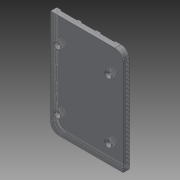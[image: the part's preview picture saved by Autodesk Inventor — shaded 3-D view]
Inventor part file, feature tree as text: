
AUTODESK INVENTOR PART (.ipt)
format: ipt  version: 2015 (Build 190159000, 159)  size: 218,624 bytes
history: native  units: mm
features: extrude x6, chamfer x5, other x4, fillet x1, shell x1, imported_body x1
ambient origin geometry x8: Origin, YZ Plane, XZ Plane, XY Plane, X Axis, Y Axis, Z Axis, Center Point
bodies: Solid1 (feature_tree)
feature tree (18):
  extrude  "baseBody"  Depth=70.0mm
  fillet  "filletBaseBody"  Radius=100.0mm
  shell  "shellBaseBody"  Thickness=50.0mm
  extrude  "borderCase"  Depth=35.0mm
  extrude  "frontHoles"  TaperAngle=0.0deg  [1 undecoded]
  extrude  "lateralHoles"  TaperAngle=0.0deg  [1 undecoded]
  other  "baseScrewHolders"
  extrude  "screwHolders"  Depth=5.0mm TaperAngle=0.0deg
  extrude  "screwHoles"  Depth=8.0mm
  chamfer  "screwHolderChamfler1"  Distance=2.0mm
  chamfer  "screwHolderChamfler2"  Distance=8.0mm
  chamfer  "screwHolderChamfler3"  Distance=1.0mm
  chamfer  "screwHolderChamfler4"  Distance=1.0mm
  chamfer  "Chamfer5"  Distance=3.0mm
  imported_body  "base"
  other  "baseBorderCase"
  other  "baseFrontHoles"
  other  "baseLateralHoles"
note: 2 required parameter values undecoded (feature->parameter linkage not recoverable at this tier; creation-order binding heuristic only, values carry confidence <= 0.55)
